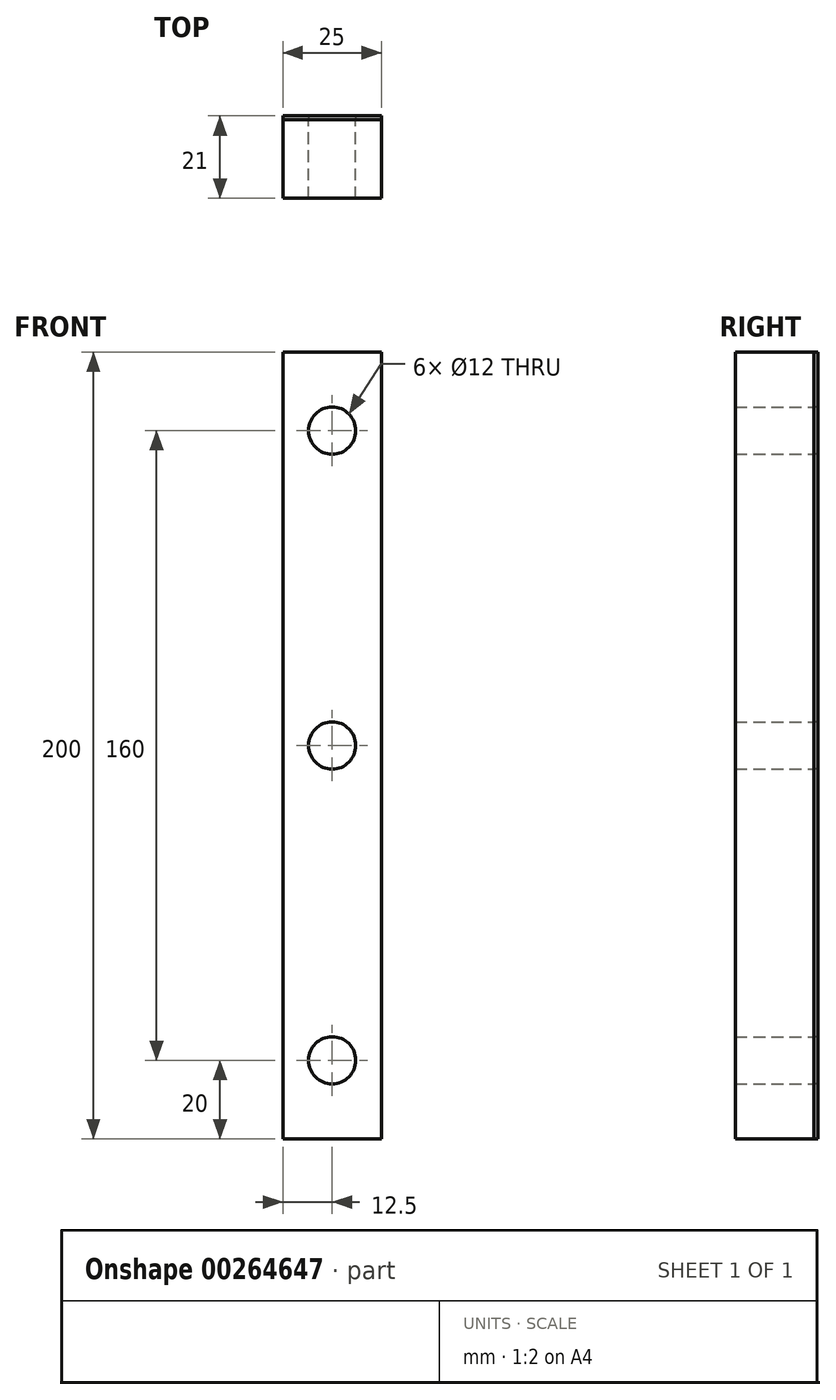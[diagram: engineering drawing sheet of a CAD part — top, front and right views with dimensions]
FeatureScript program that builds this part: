
annotation { "Feature Type Name" : "Feature", "Feature Type Description" : "" }
export const myFeature = defineFeature(function(context is Context, id is Id, definition is map)
    precondition{}
    {
        {
            var Q0;
            Q0=qCreatedBy(makeId("Front.planeOp"),FACE);
            var sketch = newSketch(context, id + "F0", { "sketchPlane" : qUnion([Q0])});
            skLineSegment(sketch, "E0.bottom", {"start": v(-12.5, 100) * mm, "end": v(12.5, 100) * mm});
            skLineSegment(sketch, "E0.top", {"start": v(-12.5, -100) * mm, "end": v(12.5, -100) * mm});
            skLineSegment(sketch, "E0.left", {"start": v(-12.5, 100) * mm, "end": v(-12.5, -100) * mm});
            skLineSegment(sketch, "E0.right", {"start": v(12.5, 100) * mm, "end": v(12.5, -100) * mm});
            skPoint(sketch, "E0.middle", {"position": v(0, 0) * mm});
            skCircle(sketch, "E1", {"center": v(0, 0) * mm, "radius": 6 * mm});
            skCircle(sketch, "E2", {"center": v(0, 80) * mm, "radius": 6 * mm});
            skCircle(sketch, "E3", {"center": v(0, -80) * mm, "radius": 6 * mm});
            skLineSegment(sketch, "E4", {"start": v(0, -80) * mm, "end": v(0, 0) * mm, "construction": true});
            skLineSegment(sketch, "E5", {"start": v(0, 0) * mm, "end": v(0, 80) * mm, "construction": true});
            skSolve(sketch);
        }
        {
            var Q0;
            Q0=makeQuery(id+"F0.imprint","IMPRINT",FACE,{"disambiguationData":[TD([[makeQuery(id+"F0.imprint","IMPRINT",EDGE,{"derivedFrom":sQuery(id+"F0.wireOp",EDGE,"E0.bottom")}),-1.0]])]});
            extrude(context, id + "F1", {"entities" : qUnion([Q0]), "depth" : 20 * mm});
        }
        {
            var Q0;
            Q0 = qSketchRegion(id + "F0", true);
            extrude(context, id + "F2", {"entities" : qUnion([Q0]), "oppositeDirection" : true, "depth" : 1 * mm});
        }
    });
